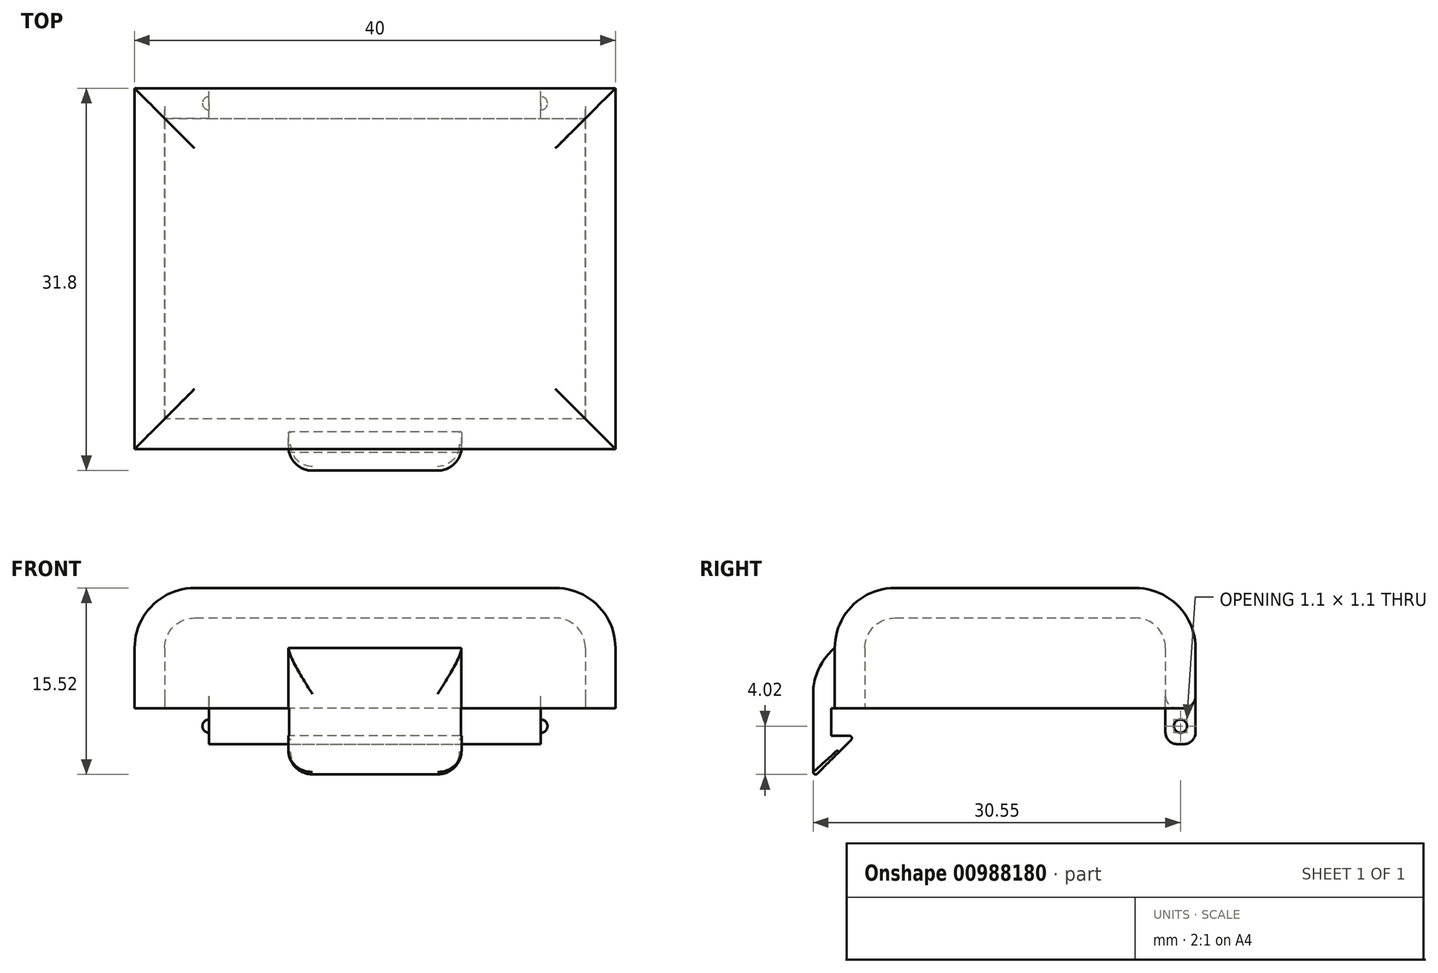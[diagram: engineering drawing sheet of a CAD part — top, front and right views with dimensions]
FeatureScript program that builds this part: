
annotation { "Feature Type Name" : "Feature", "Feature Type Description" : "" }
export const myFeature = defineFeature(function(context is Context, id is Id, definition is map)
    precondition{}
    {
        {
            var Q0;
            Q0=qCreatedBy(makeId("Top.planeOp"),FACE);
            var sketch = newSketch(context, id + "F0", { "sketchPlane" : qUnion([Q0])});
            skLineSegment(sketch, "E0.bottom", {"start": v(20, 15) * mm, "end": v(-20, 15) * mm});
            skLineSegment(sketch, "E0.top", {"start": v(20, -15) * mm, "end": v(-20, -15) * mm});
            skLineSegment(sketch, "E0.left", {"start": v(20, 15) * mm, "end": v(20, -15) * mm});
            skLineSegment(sketch, "E0.right", {"start": v(-20, 15) * mm, "end": v(-20, -15) * mm});
            skPoint(sketch, "E0.middle", {"position": v(0, 0) * mm});
            skSolve(sketch);
        }
        {
            var Q0;
            Q0 = qSketchRegion(id + "F0", true);
            extrude(context, id + "F1", {"entities" : qUnion([Q0]), "depth" : 10 * mm, "offsetDistance" : 25 * mm});
        }
        {
            var Q0;
            Q0=makeQuery(id+"F1.opExtrude","CAP_FACE",FACE,{"disambiguationData":[OSD([sQuery(id+"F0.wireOp",EDGE,"E0.bottom"),sQuery(id+"F0.wireOp",EDGE,"E0.top"),sQuery(id+"F0.wireOp",EDGE,"E0.left"),sQuery(id+"F0.wireOp",EDGE,"E0.right")])],"isStart":false});
            fillet(context, id + "F2", {"entities" : qUnion([Q0]), "radius" : 5 * mm, "tangentPropagation" : true, "allowEdgeOverflow" : false});
        }
        {
            var Q0;
            Q0=makeQuery(id+"F1.opExtrude","CAP_FACE",FACE,{"disambiguationData":[OSD([sQuery(id+"F0.wireOp",EDGE,"E0.bottom"),sQuery(id+"F0.wireOp",EDGE,"E0.top"),sQuery(id+"F0.wireOp",EDGE,"E0.left"),sQuery(id+"F0.wireOp",EDGE,"E0.right")])],"isStart":true});
            shell(context, id + "F3", {"entities" : qUnion([Q0]), "thickness" : 2.5 * mm});
        }
        {
            var Q0;
            Q0=qCreatedBy(makeId("Top.planeOp"),FACE);
            var sketch = newSketch(context, id + "F4", { "sketchPlane" : qUnion([Q0])});
            skLineSegment(sketch, "E1.0", {"start": v(17.5, 12.5) * mm, "end": v(-17.5, 12.5) * mm, "construction": true});
            skLineSegment(sketch, "E2.0", {"start": v(20, 15) * mm, "end": v(-20, 15) * mm, "construction": true});
            skPoint(sketch, "E3.0", {"position": v(0, 0) * mm});
            skLineSegment(sketch, "E4.bottom", {"start": v(-13.8, 12.5) * mm, "end": v(13.8, 12.5) * mm});
            skLineSegment(sketch, "E4.top", {"start": v(-13.8, 15) * mm, "end": v(13.8, 15) * mm});
            skLineSegment(sketch, "E4.left", {"start": v(-13.8, 12.5) * mm, "end": v(-13.8, 15) * mm});
            skLineSegment(sketch, "E4.right", {"start": v(13.8, 12.5) * mm, "end": v(13.8, 15) * mm});
            skPoint(sketch, "E5", {"position": v(0, 12.5) * mm});
            skSolve(sketch);
        }
        {
            var Q0;
            Q0 = qSketchRegion(id + "F4", true);
            extrude(context, id + "F5", {"entities" : qUnion([Q0]), "operationType" : NewBodyOperationType.ADD, "oppositeDirection" : true, "depth" : 3 * mm, "offsetDistance" : 25 * mm});
        }
        {
            var Q0;
            Q0=qCreatedBy(makeId("Top.planeOp"),FACE);
            var sketch = newSketch(context, id + "F6", { "sketchPlane" : qUnion([Q0])});
            skLineSegment(sketch, "E6.bottom", {"start": v(0, 25.94) * mm, "end": v(46.03, 25.94) * mm});
            skLineSegment(sketch, "E6.top", {"start": v(0, -43.63) * mm, "end": v(46.03, -43.63) * mm});
            skLineSegment(sketch, "E6.left", {"start": v(0, 25.94) * mm, "end": v(0, -43.63) * mm});
            skLineSegment(sketch, "E6.right", {"start": v(46.03, 25.94) * mm, "end": v(46.03, -43.63) * mm});
            skSolve(sketch);
        }
        {
            var Q0;
            Q0=makeQuery(id+"F6.imprint","IMPRINT",FACE,{"disambiguationData":[TD([[makeQuery(id+"F6.imprint","IMPRINT",EDGE,{"derivedFrom":sQuery(id+"F6.wireOp",EDGE,"E6.bottom")}),-1.0]])]});
            extrude(context, id + "F7", {"entities" : qUnion([Q0]), "operationType" : NewBodyOperationType.REMOVE, "endBound" : BoundingType.SYMMETRIC, "depth" : 25 * mm, "offsetDistance" : 25 * mm});
        }
        {
            var Q0;
            Q0=makeQuery(id+"F5.opExtrude","SWEPT_FACE",FACE,{"disambiguationData":[OSD([sQuery(id+"F4.wireOp",EDGE,"E4.left")])]});
            var sketch = newSketch(context, id + "F8", { "sketchPlane" : qUnion([Q0])});
            skLineSegment(sketch, "E7.0", {"start": v(-12.5, 0) * mm, "end": v(-15, 0) * mm, "construction": true});
            skLineSegment(sketch, "E8.0", {"start": v(-12.5, -3) * mm, "end": v(-12.5, 0) * mm, "construction": true});
            skPoint(sketch, "E9", {"position": v(-13.75, 0) * mm});
            skPoint(sketch, "E10", {"position": v(-12.5, -1.5) * mm});
            skCircle(sketch, "E11", {"center": v(-13.75, -1.5) * mm, "radius": 0.55 * mm});
            skSolve(sketch);
        }
        {
            var Q0;
            Q0 = qSketchRegion(id + "F8", true);
            extrude(context, id + "F9", {"entities" : qUnion([Q0]), "operationType" : NewBodyOperationType.ADD, "depth" : .55 * mm, "offsetDistance" : 25 * mm});
        }
        {
            var Q0;
            Q0=makeQuery(id+"F9.opExtrude","CAP_EDGE",EDGE,{"disambiguationData":[OSD([sQuery(id+"F8.wireOp",EDGE,"E11")])],"isStart":false});
            fillet(context, id + "F10", {"entities" : qUnion([Q0]), "radius" : .55 * mm, "tangentPropagation" : true, "allowEdgeOverflow" : false});
        }
        {
            var Q0;
            Q0=makeQuery(id+"F5.opExtrude","CAP_EDGE",EDGE,{"disambiguationData":[OSD([sQuery(id+"F4.wireOp",EDGE,"E4.top")])],"isStart":false});
            var Q1;
            Q1=makeQuery(id+"F5.opExtrude","CAP_EDGE",EDGE,{"disambiguationData":[OSD([sQuery(id+"F4.wireOp",EDGE,"E4.bottom")])],"isStart":false});
            var Q2;
            {var subQ0=sQuery(id+"F0.wireOp",EDGE,"E0.right");var subQ1=sQuery(id+"F0.wireOp",EDGE,"E0.bottom");Q2=makeQuery(id+"F5.boolean.opBoolean","SPLIT",EDGE,{"disambiguationData":[TD([makeQuery(id+"F1.opExtrude","SWEPT_FACE",FACE,{"disambiguationData":[OSD([subQ0])]})])],"derivedFrom":makeQuery(id+"F1.opExtrude","CAP_EDGE",EDGE,{"disambiguationData":[OSD([subQ1])],"isStart":true})});}
            var Q3;
            {var subQ1=sQuery(id+"F0.wireOp",EDGE,"E0.bottom");Q3=makeQuery(id+"F5.boolean.opBoolean","SPLIT",EDGE,{"disambiguationData":[TD([makeQuery(id+"F5.opExtrude","SWEPT_FACE",FACE,{"disambiguationData":[OSD([sQuery(id+"F4.wireOp",EDGE,"E4.left")])]})])],"derivedFrom":makeQuery(id+"F3.opShell","OFFSET_EDGE",EDGE,{"disambiguationData":[OSD([subQ1]),TDD([makeQuery(id+"F1.opExtrude","CAP_EDGE",EDGE,{"disambiguationData":[OSD([subQ1])],"isStart":true})])]})});}
            fillet(context, id + "F11", {"entities" : qUnion([Q0, Q1, Q2, Q3]), "radius" : 1 * mm, "tangentPropagation" : true, "allowEdgeOverflow" : false});
        }
        {
            var Q0;
            Q0=makeQuery(id+"F1.opExtrude","SWEPT_BODY",BODY,{"disambiguationData":[OSD([sQuery(id+"F0.wireOp",EDGE,"E0.bottom"),sQuery(id+"F0.wireOp",EDGE,"E0.top"),sQuery(id+"F0.wireOp",EDGE,"E0.left"),sQuery(id+"F0.wireOp",EDGE,"E0.right")])]});
            var Q1;
            Q1=qCreatedBy(makeId("Right.planeOp"),FACE);
            mirror(context, id + "F12", {"operationType" : NewBodyOperationType.ADD, "entities" : qUnion([Q0]), "mirrorPlane" : qUnion([Q1])});
        }
        {
            var Q0;
            {var subQ0=makeQuery(id+"F1.opExtrude","SWEPT_FACE",FACE,{"disambiguationData":[OSD([sQuery(id+"F0.wireOp",EDGE,"E0.top")])]});Q0=makeQuery(id+"F12.boolean.opBoolean","MERGE",FACE,{"derivedFrom":[subQ0,makeQuery(id+"F12.opPattern","COPY",FACE,{"derivedFrom":subQ0,"instanceName":"1"})]});}
            var sketch = newSketch(context, id + "F13", { "sketchPlane" : qUnion([Q0])});
            skLineSegment(sketch, "E12.bottom", {"start": v(7.2, 5) * mm, "end": v(-7.2, 5) * mm});
            skLineSegment(sketch, "E12.top", {"start": v(7.2, -7) * mm, "end": v(-7.2, -7) * mm});
            skLineSegment(sketch, "E12.left", {"start": v(7.2, 5) * mm, "end": v(7.2, -7) * mm});
            skLineSegment(sketch, "E12.right", {"start": v(-7.2, 5) * mm, "end": v(-7.2, -7) * mm});
            skPoint(sketch, "E12.middle", {"position": v(0, -1) * mm});
            skSolve(sketch);
        }
        {
            var Q0;
            Q0 = qSketchRegion(id + "F13", true);
            extrude(context, id + "F14", {"entities" : qUnion([Q0]), "operationType" : NewBodyOperationType.ADD, "endBound" : BoundingType.SYMMETRIC, "depth" : 3.6 * mm, "offsetDistance" : 25 * mm});
        }
        {
            var Q0;
            Q0=makeQuery(id+"F14.opExtrude","SWEPT_FACE",FACE,{"disambiguationData":[OSD([sQuery(id+"F13.wireOp",EDGE,"E12.right")])]});
            var sketch = newSketch(context, id + "F15", { "sketchPlane" : qUnion([Q0])});
            skLineSegment(sketch, "E13", {"start": v(15, 0) * mm, "end": v(15.3, 0) * mm});
            skLineSegment(sketch, "E14", {"start": v(15.3, 0) * mm, "end": v(15.3, -2.3) * mm});
            skLineSegment(sketch, "E15", {"start": v(15.3, -2.3) * mm, "end": v(13.3, -2.3) * mm});
            skLineSegment(sketch, "E16", {"start": v(13.3, -2.3) * mm, "end": v(16.8, -5.8) * mm});
            skLineSegment(sketch, "E17", {"start": v(16.8, -5.8) * mm, "end": v(16.8, -7) * mm});
            skLineSegment(sketch, "E18", {"start": v(16.8, -7) * mm, "end": v(13.2, -7) * mm});
            skLineSegment(sketch, "E19", {"start": v(13.2, -7) * mm, "end": v(13.2, 0) * mm});
            skLineSegment(sketch, "E20", {"start": v(13.2, 0) * mm, "end": v(15, 0) * mm});
            skSolve(sketch);
        }
        {
            var Q0;
            Q0 = qSketchRegion(id + "F15", true);
            extrude(context, id + "F16", {"entities" : qUnion([Q0]), "operationType" : NewBodyOperationType.REMOVE, "oppositeDirection" : true, "depth" : 25 * mm, "offsetDistance" : 25 * mm});
        }
        {
            var Q0;
            Q0=makeQuery(id+"F14.opExtrude","CAP_EDGE",EDGE,{"disambiguationData":[OSD([sQuery(id+"F13.wireOp",EDGE,"E12.right")])],"isStart":false});
            var Q1;
            Q1=makeQuery(id+"F14.opExtrude","CAP_EDGE",EDGE,{"disambiguationData":[OSD([sQuery(id+"F13.wireOp",EDGE,"E12.left")])],"isStart":false});
            fillet(context, id + "F17", {"entities" : qUnion([Q0, Q1]), "radius" : 2 * mm, "tangentPropagation" : true, "allowEdgeOverflow" : false});
        }
        {
            var Q0;
            Q0=makeQuery(id+"F14.opExtrude","CAP_EDGE",EDGE,{"disambiguationData":[OSD([sQuery(id+"F13.wireOp",EDGE,"E12.bottom")])],"isStart":false});
            fillet(context, id + "F18", {"entities" : qUnion([Q0]), "radius" : 5 * mm, "tangentPropagation" : true, "allowEdgeOverflow" : false});
        }
        {
            var Q0;
            Q0=makeQuery(id+"F16.boolean.opBoolean","COPY",FACE,{"derivedFrom":makeQuery(id+"F16.opExtrude","SWEPT_FACE",FACE,{"disambiguationData":[OSD([sQuery(id+"F15.wireOp",EDGE,"E16")])]})});
            fillet(context, id + "F19", {"entities" : qUnion([Q0]), "radius" : .2 * mm, "tangentPropagation" : true, "allowEdgeOverflow" : false});
        }
    });
